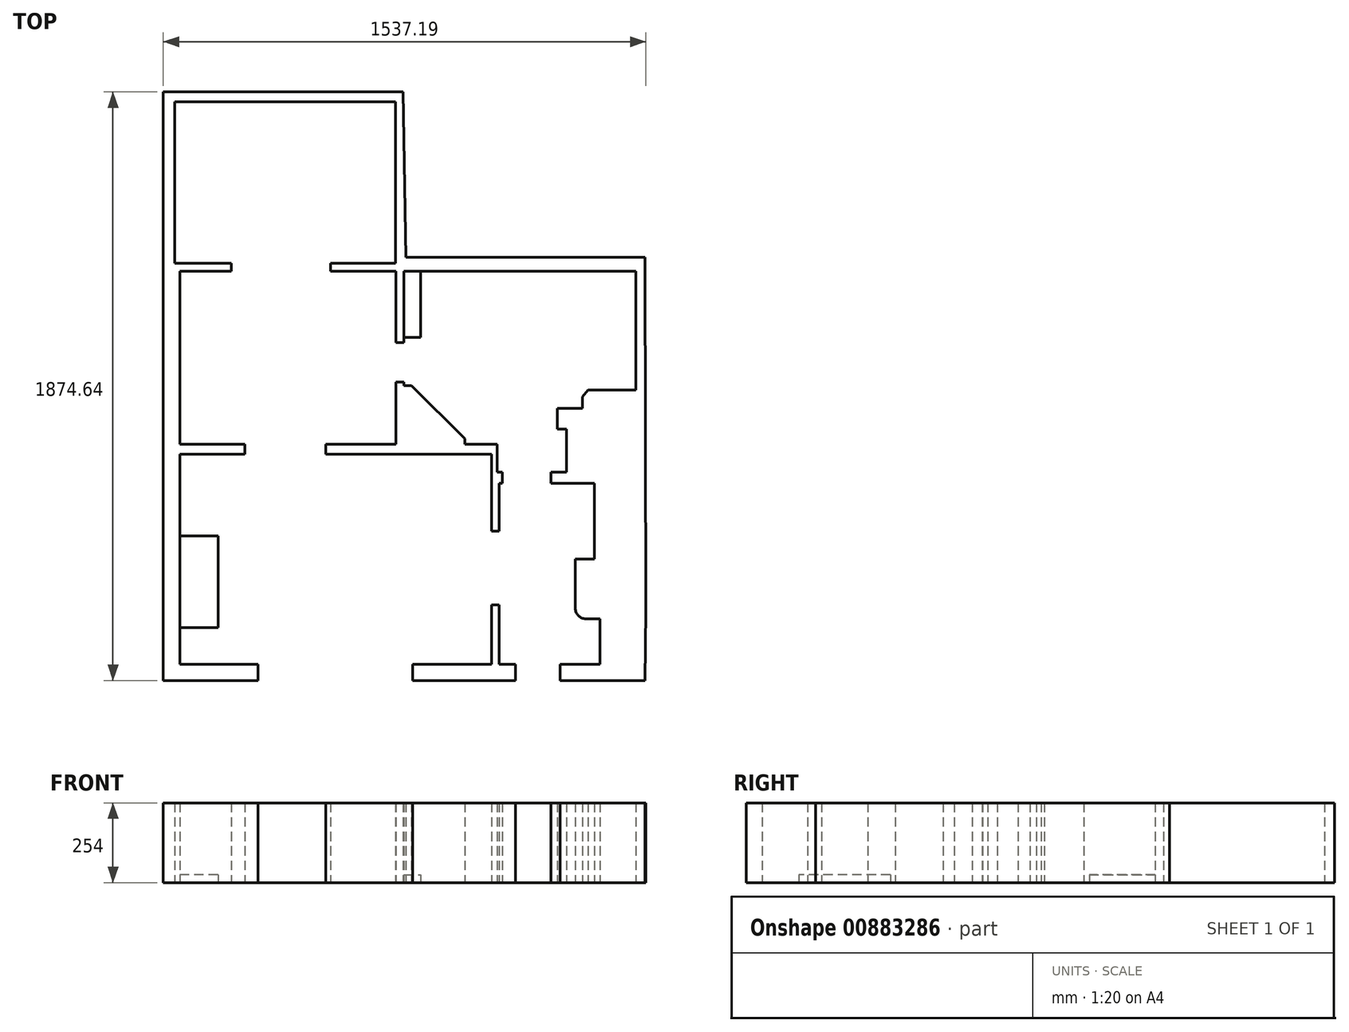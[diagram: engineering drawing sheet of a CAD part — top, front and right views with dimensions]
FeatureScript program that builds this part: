
annotation { "Feature Type Name" : "Feature", "Feature Type Description" : "" }
export const myFeature = defineFeature(function(context is Context, id is Id, definition is map)
    precondition{}
    {
        {
            var Q0;
            Q0=qCreatedBy(makeId("Top.planeOp"),FACE);
            var sketch = newSketch(context, id + "F0", { "sketchPlane" : qUnion([Q0])});
            skLineSegment(sketch, "E0", {"start": v(-1430.1, -2580.64) * mm, "end": v(1430.1, -2580.64) * mm});
            skLineSegment(sketch, "E1", {"start": v(-1430.1, -2580.64) * mm, "end": v(-1430.1, 2580.64) * mm});
            skLineSegment(sketch, "E2", {"start": v(-1430.1, 2580.64) * mm, "end": v(1430.1, 2580.64) * mm});
            skLineSegment(sketch, "E3", {"start": v(1430.1, -2580.64) * mm, "end": v(1430.1, 2580.64) * mm});
            skSolve(sketch);
        }
        {
            var Q0;
            Q0=makeQuery(id+"F0.imprint","IMPRINT",FACE,{"disambiguationData":[TD([[makeQuery(id+"F0.imprint","IMPRINT",EDGE,{"derivedFrom":sQuery(id+"F0.wireOp",EDGE,"E0")}),1.0]])]});
            var sketch = newSketch(context, id + "F1", { "sketchPlane" : qUnion([Q0])});
            skArc(sketch, "E4", {"start": v(313.58, -1103.17) * mm, "mid": v(323.5, -1127.12) * mm, "end": v(347.45, -1137.04) * mm});
            skLineSegment(sketch, "E5", {"start": v(122.4, -1333.38) * mm, "end": v(122.4, -1281.77) * mm});
            skLineSegment(sketch, "E6", {"start": v(122.4, -1281.77) * mm, "end": v(70.76, -1281.77) * mm});
            skLineSegment(sketch, "E7", {"start": v(70.76, -1281.77) * mm, "end": v(70.76, -1092.52) * mm});
            skLineSegment(sketch, "E8", {"start": v(70.76, -1092.52) * mm, "end": v(47.05, -1092.52) * mm});
            skLineSegment(sketch, "E9", {"start": v(47.05, -1092.52) * mm, "end": v(47.05, -1281.77) * mm});
            skLineSegment(sketch, "E10", {"start": v(47.05, -1281.77) * mm, "end": v(-205.2, -1281.77) * mm});
            skLineSegment(sketch, "E11", {"start": v(-205.2, -1281.77) * mm, "end": v(-205.2, -1333.38) * mm});
            skLineSegment(sketch, "E12", {"start": v(-205.2, -1333.38) * mm, "end": v(122.4, -1333.38) * mm});
            skLineSegment(sketch, "E13", {"start": v(-697.03, -1333.38) * mm, "end": v(-697.03, -1281.77) * mm});
            skLineSegment(sketch, "E14", {"start": v(-697.03, -1281.77) * mm, "end": v(-946.5, -1281.77) * mm});
            skLineSegment(sketch, "E15", {"start": v(-946.5, -1281.77) * mm, "end": v(-946.5, -612.95) * mm});
            skLineSegment(sketch, "E16", {"start": v(-946.5, -612.95) * mm, "end": v(-740.04, -612.95) * mm});
            skLineSegment(sketch, "E17", {"start": v(-740.04, -612.95) * mm, "end": v(-740.04, -587.14) * mm});
            skLineSegment(sketch, "E18", {"start": v(-962.88, -4) * mm, "end": v(-782.24, -4) * mm});
            skLineSegment(sketch, "E19", {"start": v(-962.88, -4) * mm, "end": v(-962.88, 510.02) * mm});
            skLineSegment(sketch, "E20", {"start": v(-232.92, -30.07) * mm, "end": v(506.08, -29.6) * mm});
            skLineSegment(sketch, "E21", {"start": v(-258.32, -580.78) * mm, "end": v(-481.98, -580.78) * mm});
            skLineSegment(sketch, "E22", {"start": v(-962.88, 510.02) * mm, "end": v(-259.07, 510.02) * mm});
            skLineSegment(sketch, "E23", {"start": v(-258.32, -580.78) * mm, "end": v(-258.32, -382.66) * mm});
            skLineSegment(sketch, "E24", {"start": v(-258.32, -30.24) * mm, "end": v(-466.6, -30.24) * mm});
            skLineSegment(sketch, "E25", {"start": v(-946.5, -580.78) * mm, "end": v(-946.5, -30.24) * mm});
            skLineSegment(sketch, "E26", {"start": v(-232.92, -393.66) * mm, "end": v(-232.92, -382.66) * mm});
            skLineSegment(sketch, "E27", {"start": v(64.39, -580.62) * mm, "end": v(64.39, -670.37) * mm});
            skLineSegment(sketch, "E28", {"start": v(506.08, -29.6) * mm, "end": v(506.08, -468.2) * mm});
            skLineSegment(sketch, "E29", {"start": v(-259.07, -4) * mm, "end": v(-259.07, 510.02) * mm});
            skLineSegment(sketch, "E30", {"start": v(70.76, -858.11) * mm, "end": v(70.76, -705.42) * mm});
            skLineSegment(sketch, "E31", {"start": v(70.76, -858.11) * mm, "end": v(47.05, -858.11) * mm});
            skLineSegment(sketch, "E32", {"start": v(47.05, -858.11) * mm, "end": v(47.05, -612.95) * mm});
            skLineSegment(sketch, "E33", {"start": v(47.05, -612.95) * mm, "end": v(-481.98, -612.95) * mm});
            skLineSegment(sketch, "E34", {"start": v(-481.98, -612.95) * mm, "end": v(-481.98, -580.78) * mm});
            skLineSegment(sketch, "E35", {"start": v(264.65, -1333.38) * mm, "end": v(264.65, -1281.77) * mm});
            skLineSegment(sketch, "E36", {"start": v(264.65, -1281.77) * mm, "end": v(391.65, -1281.77) * mm});
            skLineSegment(sketch, "E37", {"start": v(391.65, -1281.77) * mm, "end": v(391.65, -1110.74) * mm});
            skLineSegment(sketch, "E38", {"start": v(393.97, -1111.65) * mm, "end": v(538.02, -1111.65) * mm});
            skLineSegment(sketch, "E39", {"start": v(538.02, -1111.65) * mm, "end": v(535.7, -1333.38) * mm});
            skLineSegment(sketch, "E40", {"start": v(70.76, -705.42) * mm, "end": v(81.32, -705.42) * mm});
            skLineSegment(sketch, "E41", {"start": v(81.32, -705.42) * mm, "end": v(81.32, -670.37) * mm});
            skLineSegment(sketch, "E42", {"start": v(236.16, -670.37) * mm, "end": v(236.16, -705.42) * mm});
            skLineSegment(sketch, "E43", {"start": v(236.16, -705.42) * mm, "end": v(373.8, -705.42) * mm});
            skLineSegment(sketch, "E44", {"start": v(-824.99, -873.54) * mm, "end": v(-946.5, -873.54) * mm});
            skLineSegment(sketch, "E45", {"start": v(-824.99, -873.54) * mm, "end": v(-824.99, -1164.93) * mm});
            skLineSegment(sketch, "E46", {"start": v(-824.99, -1164.93) * mm, "end": v(-946.5, -1164.93) * mm});
            skLineSegment(sketch, "E47", {"start": v(-946.5, -873.54) * mm, "end": v(-946.5, -1164.93) * mm});
            skLineSegment(sketch, "E48", {"start": v(535.7, -1333.38) * mm, "end": v(-999.17, -1333.38) * mm});
            skLineSegment(sketch, "E49", {"start": v(-999.17, -1333.38) * mm, "end": v(-999.17, 541.26) * mm});
            skLineSegment(sketch, "E50", {"start": v(-234.64, 541.26) * mm, "end": v(-226.68, 14.98) * mm});
            skLineSegment(sketch, "E51", {"start": v(-226.68, 14.98) * mm, "end": v(535.98, 14.98) * mm});
            skLineSegment(sketch, "E52", {"start": v(535.98, 14.98) * mm, "end": v(538.02, -1111.65) * mm});
            skLineSegment(sketch, "E53", {"start": v(313.58, -946.28) * mm, "end": v(313.58, -1103.17) * mm});
            skLineSegment(sketch, "E54", {"start": v(-946.5, -580.78) * mm, "end": v(-740.04, -580.78) * mm});
            skLineSegment(sketch, "E55", {"start": v(-740.04, -580.78) * mm, "end": v(-740.04, -587.14) * mm});
            skLineSegment(sketch, "E56", {"start": v(-232.92, -30.07) * mm, "end": v(-232.92, -257.15) * mm});
            skLineSegment(sketch, "E57", {"start": v(-232.92, -257.15) * mm, "end": v(-258.32, -257.15) * mm});
            skLineSegment(sketch, "E58", {"start": v(-258.32, -257.15) * mm, "end": v(-258.32, -30.24) * mm});
            skLineSegment(sketch, "E59", {"start": v(-258.32, -382.66) * mm, "end": v(-232.92, -382.66) * mm});
            skLineSegment(sketch, "E60", {"start": v(-946.5, -30.24) * mm, "end": v(-782.24, -30.24) * mm});
            skLineSegment(sketch, "E61", {"start": v(-782.24, -30.24) * mm, "end": v(-782.24, -4) * mm});
            skLineSegment(sketch, "E62", {"start": v(-466.6, -30.24) * mm, "end": v(-466.6, -4) * mm});
            skLineSegment(sketch, "E63", {"start": v(-466.6, -4) * mm, "end": v(-259.07, -4) * mm});
            skLineSegment(sketch, "E64", {"start": v(335.93, -466.38) * mm, "end": v(256.04, -466.38) * mm});
            skLineSegment(sketch, "E65", {"start": v(347.45, -1137.04) * mm, "end": v(391.65, -1137.04) * mm});
            skLineSegment(sketch, "E66", {"start": v(-232.92, -393.66) * mm, "end": v(-208.08, -393.66) * mm});
            skLineSegment(sketch, "E67", {"start": v(-208.08, -393.66) * mm, "end": v(-38.06, -563.69) * mm});
            skLineSegment(sketch, "E68", {"start": v(-38.06, -563.69) * mm, "end": v(-38.06, -580.62) * mm});
            skLineSegment(sketch, "E69", {"start": v(-38.06, -580.62) * mm, "end": v(64.39, -580.62) * mm});
            skLineSegment(sketch, "E70", {"start": v(64.39, -670.37) * mm, "end": v(81.32, -670.37) * mm});
            skLineSegment(sketch, "E71", {"start": v(236.16, -670.37) * mm, "end": v(285.57, -670.37) * mm});
            skLineSegment(sketch, "E72", {"start": v(285.57, -670.37) * mm, "end": v(285.57, -533.2) * mm});
            skLineSegment(sketch, "E73", {"start": v(373.8, -705.42) * mm, "end": v(373.8, -946.28) * mm});
            skLineSegment(sketch, "E74", {"start": v(373.8, -946.28) * mm, "end": v(313.58, -946.28) * mm});
            skLineSegment(sketch, "E75", {"start": v(-232.92, -240.01) * mm, "end": v(-178.73, -240.01) * mm});
            skLineSegment(sketch, "E76", {"start": v(-178.73, -240.01) * mm, "end": v(-178.73, -30.04) * mm});
            skLineSegment(sketch, "E77", {"start": v(-41.57, -29.95) * mm, "end": v(-41.57, -134.94) * mm});
            skLineSegment(sketch, "E78", {"start": v(-41.57, -134.94) * mm, "end": v(339.43, -134.94) * mm});
            skLineSegment(sketch, "E79", {"start": v(339.43, -134.94) * mm, "end": v(401.09, -196.6) * mm});
            skLineSegment(sketch, "E80", {"start": v(401.09, -196.6) * mm, "end": v(401.09, -274.5) * mm});
            skLineSegment(sketch, "E81", {"start": v(401.09, -274.5) * mm, "end": v(380.86, -274.5) * mm});
            skLineSegment(sketch, "E82", {"start": v(380.86, -274.5) * mm, "end": v(380.86, -408.27) * mm});
            skLineSegment(sketch, "E83", {"start": v(506.08, -408.27) * mm, "end": v(354.52, -408.27) * mm});
            skLineSegment(sketch, "E84", {"start": v(354.52, -408.27) * mm, "end": v(335.93, -429.12) * mm});
            skLineSegment(sketch, "E85", {"start": v(335.93, -429.12) * mm, "end": v(335.93, -466.38) * mm});
            skLineSegment(sketch, "E86", {"start": v(256.04, -466.38) * mm, "end": v(256.04, -533.2) * mm});
            skLineSegment(sketch, "E87", {"start": v(256.04, -533.2) * mm, "end": v(285.57, -533.2) * mm});
            skLineSegment(sketch, "E88", {"start": v(-999.17, 541.26) * mm, "end": v(-234.64, 541.26) * mm});
            skSolve(sketch);
        }
        {
            var Q0;
            Q0=makeQuery(id+"F1.imprint","IMPRINT",FACE,{"disambiguationData":[TD([[makeQuery(id+"F1.imprint","IMPRINT",EDGE,{"derivedFrom":sQuery(id+"F1.wireOp",EDGE,"E4")}),1.0]])]});
            var Q1;
            Q1=makeQuery(id+"F1.imprint","IMPRINT",FACE,{"disambiguationData":[TD([[makeQuery(id+"F1.imprint","IMPRINT",EDGE,{"derivedFrom":sQuery(id+"F1.wireOp",EDGE,"E21")}),1.0]])]});
            var Q2;
            {var subQ1=sQuery(id+"F1.wireOp",EDGE,"E5");Q2=makeQuery(id+"F1.imprint","IMPRINT",FACE,{"disambiguationData":[TD([[makeQuery(id+"F1.imprint","IMPRINT",EDGE,{"derivedFrom":subQ1}),1.0]])]});}
            extrude(context, id + "F2", {"entities" : qUnion([Q0, Q1, Q2]), "depth" : 254 * mm, "offsetDistance" : 25.4 * mm});
        }
        {
            var Q0;
            {var subQ0=sQuery(id+"F1.wireOp",EDGE,"E77");Q0=makeQuery(id+"F1.imprint","IMPRINT",FACE,{"disambiguationData":[TD([[makeQuery(id+"F1.imprint","IMPRINT",EDGE,{"derivedFrom":subQ0}),1.0]])]});}
            var Q1;
            {var subQ4=sQuery(id+"F1.wireOp",EDGE,"E75");Q1=makeQuery(id+"F1.imprint","IMPRINT",FACE,{"disambiguationData":[TD([[makeQuery(id+"F1.imprint","IMPRINT",EDGE,{"derivedFrom":subQ4}),1.0]])]});}
            extrude(context, id + "F3", {"entities" : qUnion([Q0, Q1]), "depth" : 25.4 * mm, "offsetDistance" : 25.4 * mm});
        }
        {
            var Q0;
            Q0=makeQuery(id+"F1.imprint","IMPRINT",FACE,{"disambiguationData":[TD([[makeQuery(id+"F1.imprint","IMPRINT",EDGE,{"derivedFrom":sQuery(id+"F1.wireOp",EDGE,"E44")}),1.0]])]});
            extrude(context, id + "F4", {"entities" : qUnion([Q0]), "depth" : 25.4 * mm, "offsetDistance" : 25.4 * mm});
        }
    });
